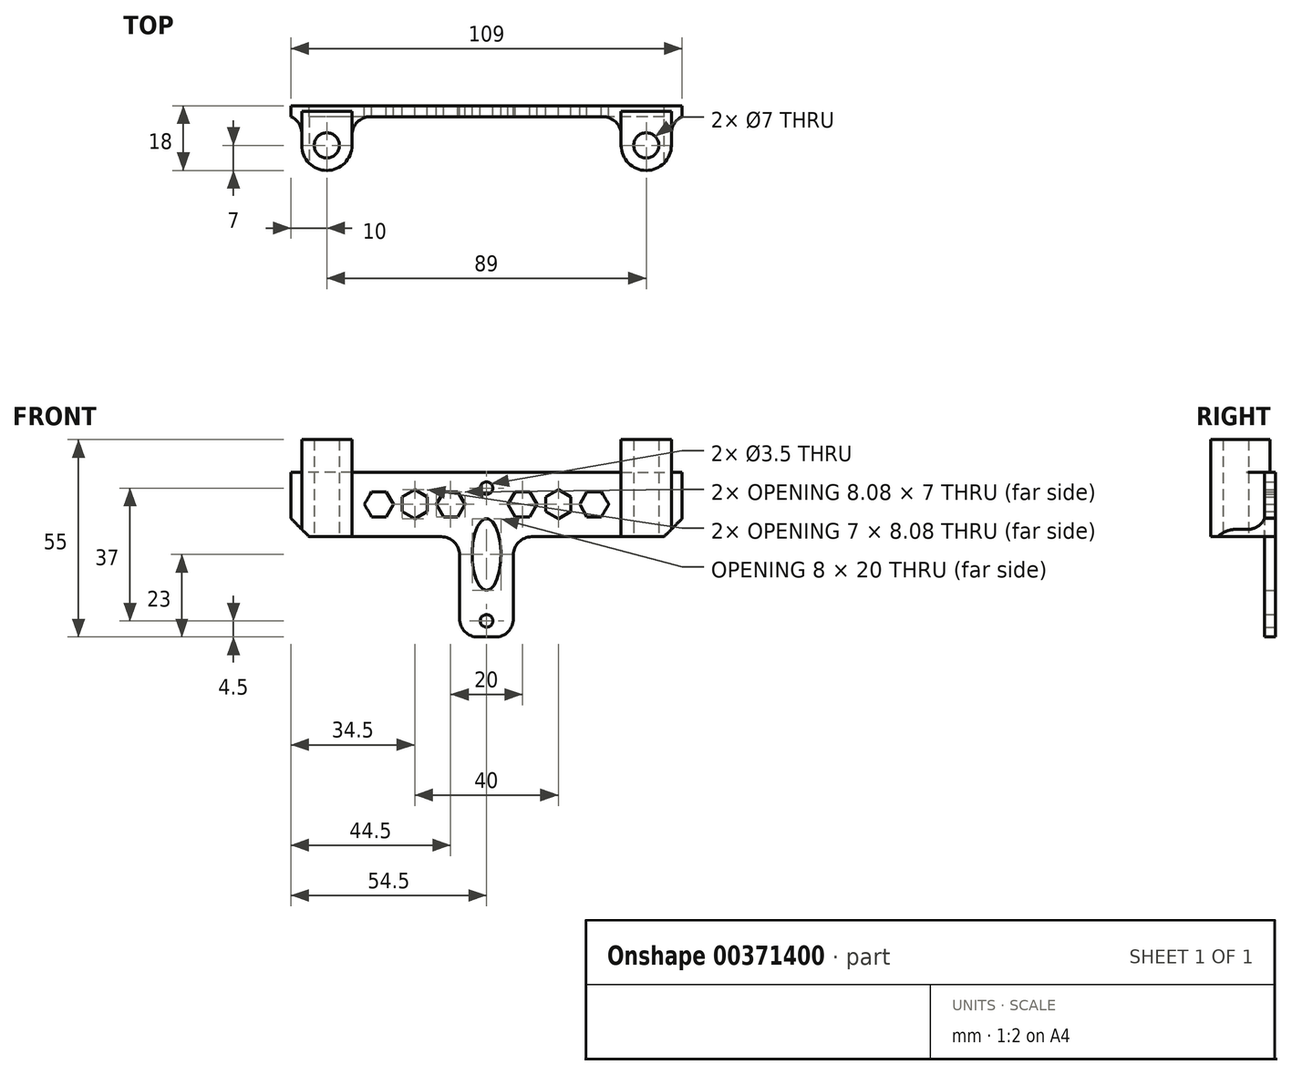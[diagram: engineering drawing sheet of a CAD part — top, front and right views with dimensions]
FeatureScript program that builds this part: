
annotation { "Feature Type Name" : "Feature", "Feature Type Description" : "" }
export const myFeature = defineFeature(function(context is Context, id is Id, definition is map)
    precondition{}
    {
        {
            var Q0;
            Q0=qCreatedBy(makeId("Front.planeOp"),FACE);
            var sketch = newSketch(context, id + "F0", { "sketchPlane" : qUnion([Q0])});
            skLineSegment(sketch, "E0", {"start": v(-54.5, -0.06) * mm, "end": v(-54.5, 8.94) * mm});
            skLineSegment(sketch, "E1", {"start": v(-54.5, -0.06) * mm, "end": v(-54.5, -9.06) * mm});
            skLineSegment(sketch, "E2", {"start": v(-54.5, 8.94) * mm, "end": v(0, 8.94) * mm});
            skLineSegment(sketch, "E3.bottom", {"start": v(0, 8.94) * mm, "end": v(-54.5, 8.94) * mm});
            skLineSegment(sketch, "E3.top", {"start": v(0, -9.06) * mm, "end": v(-54.5, -9.06) * mm});
            skLineSegment(sketch, "E3.left", {"start": v(0, 8.94) * mm, "end": v(0, -9.06) * mm});
            skLineSegment(sketch, "E3.right", {"start": v(-54.5, 8.94) * mm, "end": v(-54.5, -9.06) * mm});
            skLineSegment(sketch, "E4.MirrorCS", {"start": v(54.5, 8.94) * mm, "end": v(0, 8.94) * mm});
            skLineSegment(sketch, "E5.MirrorCS", {"start": v(54.5, -0.06) * mm, "end": v(54.5, 8.94) * mm});
            skLineSegment(sketch, "E6.MirrorCS", {"start": v(54.5, -0.06) * mm, "end": v(54.5, -9.06) * mm});
            skLineSegment(sketch, "E7.MirrorCS", {"start": v(0, 8.94) * mm, "end": v(54.5, 8.94) * mm});
            skLineSegment(sketch, "E8.MirrorCS", {"start": v(54.5, 8.94) * mm, "end": v(54.5, -9.06) * mm});
            skLineSegment(sketch, "E9.MirrorCS", {"start": v(0, -9.06) * mm, "end": v(54.5, -9.06) * mm});
            skSolve(sketch);
        }
        {
            var Q0;
            Q0 = qSketchRegion(id + "F0", true);
            extrude(context, id + "F1", {"entities" : qUnion([Q0]), "endBound" : BoundingType.SYMMETRIC, "depth" : 3 * mm});
        }
        {
            var Q0;
            Q0=qCreatedBy(makeId("Top.planeOp"),FACE);
            var sketch = newSketch(context, id + "F2", { "sketchPlane" : qUnion([Q0])});
            skCircle(sketch, "E10", {"center": v(-44.5, -9.5) * mm, "radius": 3.5 * mm});
            skCircle(sketch, "E11", {"center": v(-44.5, -9.5) * mm, "radius": 7 * mm});
            skLineSegment(sketch, "E12", {"start": v(-51.5, -9.5) * mm, "end": v(-51.5, 0) * mm});
            skLineSegment(sketch, "E13", {"start": v(-37.5, -9.5) * mm, "end": v(-37.5, 0) * mm});
            skLineSegment(sketch, "E14", {"start": v(-51.5, 0) * mm, "end": v(-37.5, 0) * mm});
            skPoint(sketch, "E15.MirrorP", {"position": v(44.5, -9.5) * mm});
            skLineSegment(sketch, "E16.MirrorCS", {"start": v(37.5, -9.5) * mm, "end": v(37.5, 0) * mm});
            skCircle(sketch, "E17.MirrorC", {"center": v(44.5, -9.5) * mm, "radius": 7 * mm});
            skLineSegment(sketch, "E18.MirrorCS", {"start": v(51.5, -9.5) * mm, "end": v(51.5, 0) * mm});
            skLineSegment(sketch, "E19.MirrorCS", {"start": v(51.5, 0) * mm, "end": v(37.5, 0) * mm});
            skCircle(sketch, "E20.MirrorC", {"center": v(44.5, -9.5) * mm, "radius": 3.5 * mm});
            skSolve(sketch);
        }
        {
            var Q0;
            Q0 = qSketchRegion(id + "F2", true);
            extrude(context, id + "F3", {"entities" : qUnion([Q0]), "operationType" : NewBodyOperationType.ADD, "endBound" : BoundingType.SYMMETRIC, "depth" : 18 * mm});
        }
        {
            var Q0;
            Q0=makeQuery(id+"F3.opExtrude","CAP_FACE",FACE,{"disambiguationData":[OSD([sQuery(id+"F2.wireOp",EDGE,"E10"),sQuery(id+"F2.wireOp",EDGE,"E11"),sQuery(id+"F2.wireOp",EDGE,"E12"),sQuery(id+"F2.wireOp",EDGE,"E13"),sQuery(id+"F2.wireOp",EDGE,"E14")])],"isStart":false});
            var Q1;
            Q1=makeQuery(id+"F3.opExtrude","CAP_FACE",FACE,{"disambiguationData":[OSD([sQuery(id+"F2.wireOp",EDGE,"E16.MirrorCS"),sQuery(id+"F2.wireOp",EDGE,"E17.MirrorC"),sQuery(id+"F2.wireOp",EDGE,"E18.MirrorCS"),sQuery(id+"F2.wireOp",EDGE,"E19.MirrorCS"),sQuery(id+"F2.wireOp",EDGE,"E20.MirrorC")])],"isStart":false});
            extrude(context, id + "F4", {"entities" : qUnion([Q0, Q1]), "operationType" : NewBodyOperationType.ADD, "oppositeDirection" : true, "depth" : -9 * mm});
        }
        {
            var Q0;
            Q0=qCreatedBy(makeId("Front.planeOp"),FACE);
            var sketch = newSketch(context, id + "F5", { "sketchPlane" : qUnion([Q0])});
            skLineSegment(sketch, "E21", {"start": v(0, 0) * mm, "end": v(0, -37) * mm});
            skLineSegment(sketch, "E22", {"start": v(0, -37) * mm, "end": v(-7.5, -37) * mm});
            skLineSegment(sketch, "E23", {"start": v(-7.5, -37) * mm, "end": v(7.5, -37) * mm});
            skLineSegment(sketch, "E24", {"start": v(-7.5, -37) * mm, "end": v(-7.5, 0) * mm});
            skLineSegment(sketch, "E25", {"start": v(7.5, -37) * mm, "end": v(7.5, 0) * mm});
            skLineSegment(sketch, "E26", {"start": v(7.5, 0) * mm, "end": v(-7.5, 0) * mm});
            skSolve(sketch);
        }
        {
            var Q0;
            Q0 = qSketchRegion(id + "F5", true);
            extrude(context, id + "F6", {"entities" : qUnion([Q0]), "operationType" : NewBodyOperationType.ADD, "endBound" : BoundingType.SYMMETRIC, "depth" : 3 * mm});
        }
        {
            var Q0;
            Q0=qCreatedBy(makeId("Front.planeOp"),FACE);
            var sketch = newSketch(context, id + "F7", { "sketchPlane" : qUnion([Q0])});
            skLineSegment(sketch, "E27", {"start": v(0, 0) * mm, "end": v(0, -14) * mm});
            skLineSegment(sketch, "E28", {"start": v(0, 0) * mm, "end": v(0, 4.5) * mm});
            skLineSegment(sketch, "E29", {"start": v(0, -14) * mm, "end": v(0, -32.5) * mm});
            skCircle(sketch, "E30", {"center": v(0, -32.5) * mm, "radius": 1.75 * mm});
            skCircle(sketch, "E31", {"center": v(0, 4.5) * mm, "radius": 1.75 * mm});
            skEllipse(sketch, "E32", {"center": v(0, -14) * mm, "majorRadius": 10 * mm, "minorRadius": 4 * mm, "majorAxis": v(0, -1)});
            skSolve(sketch);
        }
        {
            var Q0;
            Q0 = qSketchRegion(id + "F7", true);
            extrude(context, id + "F8", {"entities" : qUnion([Q0]), "operationType" : NewBodyOperationType.REMOVE, "endBound" : BoundingType.SYMMETRIC, "depth" : 25.4 * mm});
        }
        {
            var Q0;
            Q0=makeQuery(id+"F6.opExtrude","SWEPT_EDGE",EDGE,{"disambiguationData":[OSD([sQuery(id+"F5.wireOp",EDGE,"E23"),sQuery(id+"F5.wireOp",EDGE,"E25")])]});
            var Q1;
            Q1=makeQuery(id+"F6.opExtrude","SWEPT_EDGE",EDGE,{"disambiguationData":[OSD([sQuery(id+"F5.wireOp",EDGE,"E23"),sQuery(id+"F5.wireOp",EDGE,"E24")])]});
            var Q2;
            Q2=makeQuery(id+"F6.boolean.opBoolean","INTERSECT",EDGE,{"derivedFrom":[makeQuery(id+"F1.opExtrude","SWEPT_FACE",FACE,{"disambiguationData":[OSD([sQuery(id+"F0.wireOp",EDGE,"E3.top"),sQuery(id+"F0.wireOp",EDGE,"E9.MirrorCS")])]}),makeQuery(id+"F6.opExtrude","SWEPT_FACE",FACE,{"disambiguationData":[OSD([sQuery(id+"F5.wireOp",EDGE,"E24")])]})]});
            var Q3;
            Q3=makeQuery(id+"F6.boolean.opBoolean","INTERSECT",EDGE,{"derivedFrom":[makeQuery(id+"F1.opExtrude","SWEPT_FACE",FACE,{"disambiguationData":[OSD([sQuery(id+"F0.wireOp",EDGE,"E3.top"),sQuery(id+"F0.wireOp",EDGE,"E9.MirrorCS")])]}),makeQuery(id+"F6.opExtrude","SWEPT_FACE",FACE,{"disambiguationData":[OSD([sQuery(id+"F5.wireOp",EDGE,"E25")])]})]});
            var Q4;
            Q4=makeQuery(id+"F3.boolean.opBoolean","INTERSECT",EDGE,{"derivedFrom":[makeQuery(id+"F1.opExtrude","CAP_FACE",FACE,{"disambiguationData":[OSD([sQuery(id+"F0.wireOp",EDGE,"E3.bottom"),sQuery(id+"F0.wireOp",EDGE,"E3.top"),sQuery(id+"F0.wireOp",EDGE,"E3.right"),sQuery(id+"F0.wireOp",EDGE,"E7.MirrorCS"),sQuery(id+"F0.wireOp",EDGE,"E8.MirrorCS"),sQuery(id+"F0.wireOp",EDGE,"E9.MirrorCS")])],"isStart":false}),makeQuery(id+"F3.opExtrude","SWEPT_FACE",FACE,{"disambiguationData":[OSD([sQuery(id+"F2.wireOp",EDGE,"E12")])]})]});
            var Q5;
            Q5=makeQuery(id+"F3.boolean.opBoolean","INTERSECT",EDGE,{"derivedFrom":[makeQuery(id+"F1.opExtrude","CAP_FACE",FACE,{"disambiguationData":[OSD([sQuery(id+"F0.wireOp",EDGE,"E3.bottom"),sQuery(id+"F0.wireOp",EDGE,"E3.top"),sQuery(id+"F0.wireOp",EDGE,"E3.right"),sQuery(id+"F0.wireOp",EDGE,"E7.MirrorCS"),sQuery(id+"F0.wireOp",EDGE,"E8.MirrorCS"),sQuery(id+"F0.wireOp",EDGE,"E9.MirrorCS")])],"isStart":false}),makeQuery(id+"F3.opExtrude","SWEPT_FACE",FACE,{"disambiguationData":[OSD([sQuery(id+"F2.wireOp",EDGE,"E13")])]})]});
            var Q6;
            Q6=makeQuery(id+"F3.boolean.opBoolean","INTERSECT",EDGE,{"derivedFrom":[makeQuery(id+"F1.opExtrude","CAP_FACE",FACE,{"disambiguationData":[OSD([sQuery(id+"F0.wireOp",EDGE,"E3.bottom"),sQuery(id+"F0.wireOp",EDGE,"E3.top"),sQuery(id+"F0.wireOp",EDGE,"E3.right"),sQuery(id+"F0.wireOp",EDGE,"E7.MirrorCS"),sQuery(id+"F0.wireOp",EDGE,"E8.MirrorCS"),sQuery(id+"F0.wireOp",EDGE,"E9.MirrorCS")])],"isStart":false}),makeQuery(id+"F3.opExtrude","SWEPT_FACE",FACE,{"disambiguationData":[OSD([sQuery(id+"F2.wireOp",EDGE,"E18.MirrorCS")])]})]});
            var Q7;
            Q7=makeQuery(id+"F3.boolean.opBoolean","INTERSECT",EDGE,{"derivedFrom":[makeQuery(id+"F1.opExtrude","CAP_FACE",FACE,{"disambiguationData":[OSD([sQuery(id+"F0.wireOp",EDGE,"E3.bottom"),sQuery(id+"F0.wireOp",EDGE,"E3.top"),sQuery(id+"F0.wireOp",EDGE,"E3.right"),sQuery(id+"F0.wireOp",EDGE,"E7.MirrorCS"),sQuery(id+"F0.wireOp",EDGE,"E8.MirrorCS"),sQuery(id+"F0.wireOp",EDGE,"E9.MirrorCS")])],"isStart":false}),makeQuery(id+"F3.opExtrude","SWEPT_FACE",FACE,{"disambiguationData":[OSD([sQuery(id+"F2.wireOp",EDGE,"E16.MirrorCS")])]})]});
            var Q8;
            Q8=makeQuery(id+"F3.boolean.opBoolean","INTERSECT",EDGE,{"derivedFrom":[makeQuery(id+"F1.opExtrude","SWEPT_FACE",FACE,{"disambiguationData":[OSD([sQuery(id+"F0.wireOp",EDGE,"E3.bottom"),sQuery(id+"F0.wireOp",EDGE,"E7.MirrorCS")])]}),makeQuery(id+"F3.opExtrude","SWEPT_FACE",FACE,{"disambiguationData":[OSD([sQuery(id+"F2.wireOp",EDGE,"E19.MirrorCS")])]})]});
            var Q9;
            Q9=makeQuery(id+"F3.boolean.opBoolean","INTERSECT",EDGE,{"derivedFrom":[makeQuery(id+"F1.opExtrude","SWEPT_FACE",FACE,{"disambiguationData":[OSD([sQuery(id+"F0.wireOp",EDGE,"E3.bottom"),sQuery(id+"F0.wireOp",EDGE,"E7.MirrorCS")])]}),makeQuery(id+"F3.opExtrude","SWEPT_FACE",FACE,{"disambiguationData":[OSD([sQuery(id+"F2.wireOp",EDGE,"E14")])]})]});
            fillet(context, id + "F9", {"entities" : qUnion([Q0, Q1, Q2, Q3, Q4, Q5, Q6, Q7, Q8, Q9]), "radius" : 5.08 * mm, "tangentPropagation" : true, "allowEdgeOverflow" : false});
        }
        {
            var Q0;
            Q0=makeQuery(id+"F1.opExtrude","SWEPT_EDGE",EDGE,{"disambiguationData":[OSD([sQuery(id+"F0.wireOp",EDGE,"E3.top"),sQuery(id+"F0.wireOp",EDGE,"E3.right")])]});
            var Q1;
            Q1=makeQuery(id+"F1.opExtrude","SWEPT_EDGE",EDGE,{"disambiguationData":[OSD([sQuery(id+"F0.wireOp",EDGE,"E3.bottom"),sQuery(id+"F0.wireOp",EDGE,"E3.right")])]});
            var Q2;
            Q2=makeQuery(id+"F1.opExtrude","SWEPT_EDGE",EDGE,{"disambiguationData":[OSD([sQuery(id+"F0.wireOp",EDGE,"E7.MirrorCS"),sQuery(id+"F0.wireOp",EDGE,"E8.MirrorCS")])]});
            var Q3;
            Q3=makeQuery(id+"F1.opExtrude","SWEPT_EDGE",EDGE,{"disambiguationData":[OSD([sQuery(id+"F0.wireOp",EDGE,"E8.MirrorCS"),sQuery(id+"F0.wireOp",EDGE,"E9.MirrorCS")])]});
            chamfer(context, id + "F10", {"entities" : qUnion([Q0, Q1, Q2, Q3]), "width" : 5.08 * mm, "tangentPropagation" : true});
        }
        {
            var Q0;
            Q0=qCreatedBy(makeId("Front.planeOp"),FACE);
            var sketch = newSketch(context, id + "F11", { "sketchPlane" : qUnion([Q0])});
            skLineSegment(sketch, "E33", {"start": v(0, 0) * mm, "end": v(-10, 0) * mm});
            skLineSegment(sketch, "E34", {"start": v(-10, 0) * mm, "end": v(-20, 0) * mm});
            skLineSegment(sketch, "E35", {"start": v(-20, 0) * mm, "end": v(-30, 0) * mm});
            skCircle(sketch, "E36.cCircle", {"center": v(-30, 0) * mm, "radius": 3.5 * mm, "construction": true});
            skLineSegment(sketch, "E36.0", {"start": v(-32.02, 3.5) * mm, "end": v(-27.98, 3.5) * mm});
            skLineSegment(sketch, "E36.1", {"start": v(-27.98, 3.5) * mm, "end": v(-25.96, 0) * mm});
            skLineSegment(sketch, "E36.2", {"start": v(-25.96, 0) * mm, "end": v(-27.98, -3.5) * mm});
            skLineSegment(sketch, "E36.3", {"start": v(-27.98, -3.5) * mm, "end": v(-32.02, -3.5) * mm});
            skLineSegment(sketch, "E36.4", {"start": v(-32.02, -3.5) * mm, "end": v(-34.04, 0) * mm});
            skLineSegment(sketch, "E36.5", {"start": v(-34.04, 0) * mm, "end": v(-32.02, 3.5) * mm});
            skPoint(sketch, "E36.0.midPoint", {"position": v(-30, 3.5) * mm});
            skCircle(sketch, "E37.cCircle", {"center": v(-20, 0) * mm, "radius": 3.5 * mm, "construction": true});
            skLineSegment(sketch, "E37.0", {"start": v(-23.5, -2.02) * mm, "end": v(-23.5, 2.02) * mm});
            skLineSegment(sketch, "E37.1", {"start": v(-23.5, 2.02) * mm, "end": v(-20, 4.04) * mm});
            skLineSegment(sketch, "E37.2", {"start": v(-20, 4.04) * mm, "end": v(-16.5, 2.02) * mm});
            skLineSegment(sketch, "E37.3", {"start": v(-16.5, 2.02) * mm, "end": v(-16.5, -2.02) * mm});
            skLineSegment(sketch, "E37.4", {"start": v(-16.5, -2.02) * mm, "end": v(-20, -4.04) * mm});
            skLineSegment(sketch, "E37.5", {"start": v(-20, -4.04) * mm, "end": v(-23.5, -2.02) * mm});
            skPoint(sketch, "E37.0.midPoint", {"position": v(-23.5, 0) * mm});
            skCircle(sketch, "E38.cCircle", {"center": v(-10, 0) * mm, "radius": 3.5 * mm, "construction": true});
            skLineSegment(sketch, "E38.0", {"start": v(-12.02, 3.5) * mm, "end": v(-7.98, 3.5) * mm});
            skLineSegment(sketch, "E38.1", {"start": v(-7.98, 3.5) * mm, "end": v(-5.96, 0) * mm});
            skLineSegment(sketch, "E38.2", {"start": v(-5.96, 0) * mm, "end": v(-7.98, -3.5) * mm});
            skLineSegment(sketch, "E38.3", {"start": v(-7.98, -3.5) * mm, "end": v(-12.02, -3.5) * mm});
            skLineSegment(sketch, "E38.4", {"start": v(-12.02, -3.5) * mm, "end": v(-14.04, 0) * mm});
            skLineSegment(sketch, "E38.5", {"start": v(-14.04, 0) * mm, "end": v(-12.02, 3.5) * mm});
            skPoint(sketch, "E38.0.midPoint", {"position": v(-10, 3.5) * mm});
            skLineSegment(sketch, "E39.MirrorCS", {"start": v(32.02, 3.5) * mm, "end": v(27.98, 3.5) * mm});
            skLineSegment(sketch, "E40.MirrorCS", {"start": v(23.5, -2.02) * mm, "end": v(23.5, 2.02) * mm});
            skLineSegment(sketch, "E41.MirrorCS", {"start": v(12.02, 3.5) * mm, "end": v(7.98, 3.5) * mm});
            skLineSegment(sketch, "E42.MirrorCS", {"start": v(23.5, 2.02) * mm, "end": v(20, 4.04) * mm});
            skLineSegment(sketch, "E43.MirrorCS", {"start": v(16.5, 2.02) * mm, "end": v(16.5, -2.02) * mm});
            skLineSegment(sketch, "E44.MirrorCS", {"start": v(34.04, 0) * mm, "end": v(32.02, 3.5) * mm});
            skLineSegment(sketch, "E45.MirrorCS", {"start": v(32.02, -3.5) * mm, "end": v(34.04, 0) * mm});
            skLineSegment(sketch, "E46.MirrorCS", {"start": v(27.98, -3.5) * mm, "end": v(32.02, -3.5) * mm});
            skLineSegment(sketch, "E47.MirrorCS", {"start": v(25.96, 0) * mm, "end": v(27.98, -3.5) * mm});
            skLineSegment(sketch, "E48.MirrorCS", {"start": v(27.98, 3.5) * mm, "end": v(25.96, 0) * mm});
            skCircle(sketch, "E49.MirrorC", {"center": v(30, 0) * mm, "radius": 3.5 * mm, "construction": true});
            skCircle(sketch, "E50.MirrorC", {"center": v(20, 0) * mm, "radius": 3.5 * mm, "construction": true});
            skLineSegment(sketch, "E51.MirrorCS", {"start": v(20, -4.04) * mm, "end": v(23.5, -2.02) * mm});
            skPoint(sketch, "E52.MirrorP", {"position": v(23.5, 0) * mm});
            skLineSegment(sketch, "E53.MirrorCS", {"start": v(12.02, -3.5) * mm, "end": v(14.04, 0) * mm});
            skPoint(sketch, "E54.MirrorP", {"position": v(30, 3.5) * mm});
            skLineSegment(sketch, "E55.MirrorCS", {"start": v(5.96, 0) * mm, "end": v(7.98, -3.5) * mm});
            skLineSegment(sketch, "E56.MirrorCS", {"start": v(14.04, 0) * mm, "end": v(12.02, 3.5) * mm});
            skLineSegment(sketch, "E57.MirrorCS", {"start": v(7.98, 3.5) * mm, "end": v(5.96, 0) * mm});
            skPoint(sketch, "E58.MirrorP", {"position": v(10, 3.5) * mm});
            skLineSegment(sketch, "E59.MirrorCS", {"start": v(16.5, -2.02) * mm, "end": v(20, -4.04) * mm});
            skLineSegment(sketch, "E60.MirrorCS", {"start": v(7.98, -3.5) * mm, "end": v(12.02, -3.5) * mm});
            skLineSegment(sketch, "E61.MirrorCS", {"start": v(20, 4.04) * mm, "end": v(16.5, 2.02) * mm});
            skCircle(sketch, "E62.MirrorC", {"center": v(10, 0) * mm, "radius": 3.5 * mm, "construction": true});
            skSolve(sketch);
        }
        {
            var Q0;
            Q0 = qSketchRegion(id + "F11", true);
            extrude(context, id + "F12", {"entities" : qUnion([Q0]), "operationType" : NewBodyOperationType.REMOVE, "endBound" : BoundingType.SYMMETRIC, "depth" : 10 * mm});
        }
    });
